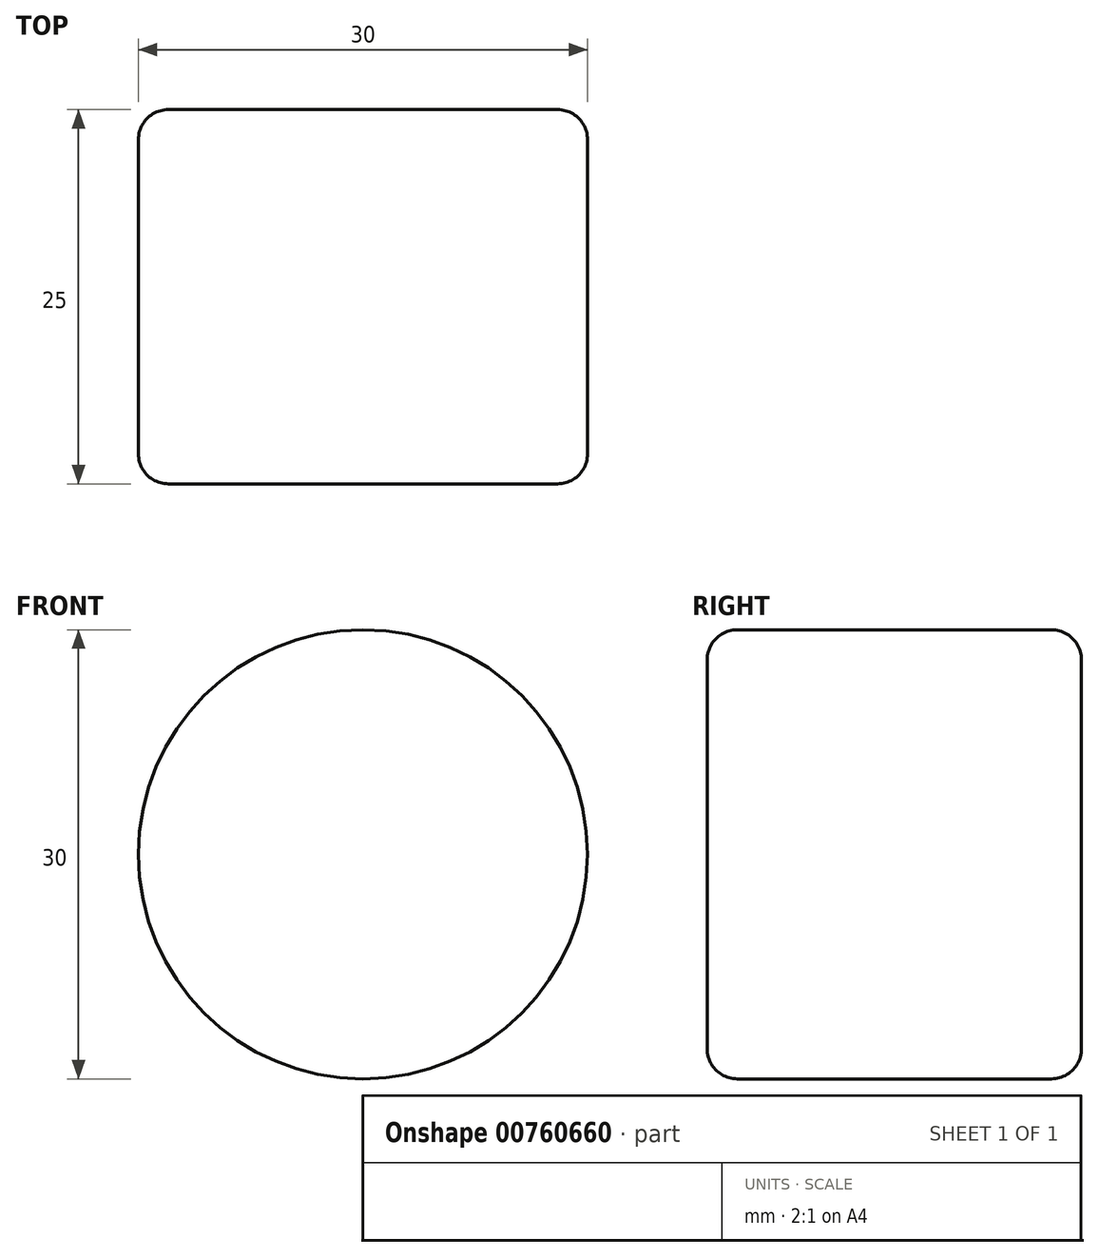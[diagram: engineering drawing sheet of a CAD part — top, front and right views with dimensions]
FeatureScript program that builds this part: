
annotation { "Feature Type Name" : "Feature", "Feature Type Description" : "" }
export const myFeature = defineFeature(function(context is Context, id is Id, definition is map)
    precondition{}
    {
        {
            var Q0;
            Q0=qCreatedBy(makeId("Front.planeOp"),FACE);
            var sketch = newSketch(context, id + "F0", { "sketchPlane" : qUnion([Q0])});
            skCircle(sketch, "E0", {"center": v(0, 0) * mm, "radius": 15 * mm});
            skSolve(sketch);
        }
        {
            var Q0;
            Q0 = qSketchRegion(id + "F0", true);
            extrude(context, id + "F1", {"entities" : qUnion([Q0]), "endBound" : BoundingType.SYMMETRIC, "depth" : 25 * mm, "offsetDistance" : 25 * mm});
        }
        {
            var Q0;
            Q0=makeQuery(id+"F1.opExtrude","SWEPT_FACE",FACE,{"disambiguationData":[OSD([sQuery(id+"F0.wireOp",EDGE,"E0")])]});
            fillet(context, id + "F2", {"entities" : qUnion([Q0]), "radius" : 2 * mm, "tangentPropagation" : true, "allowEdgeOverflow" : false});
        }
    });
